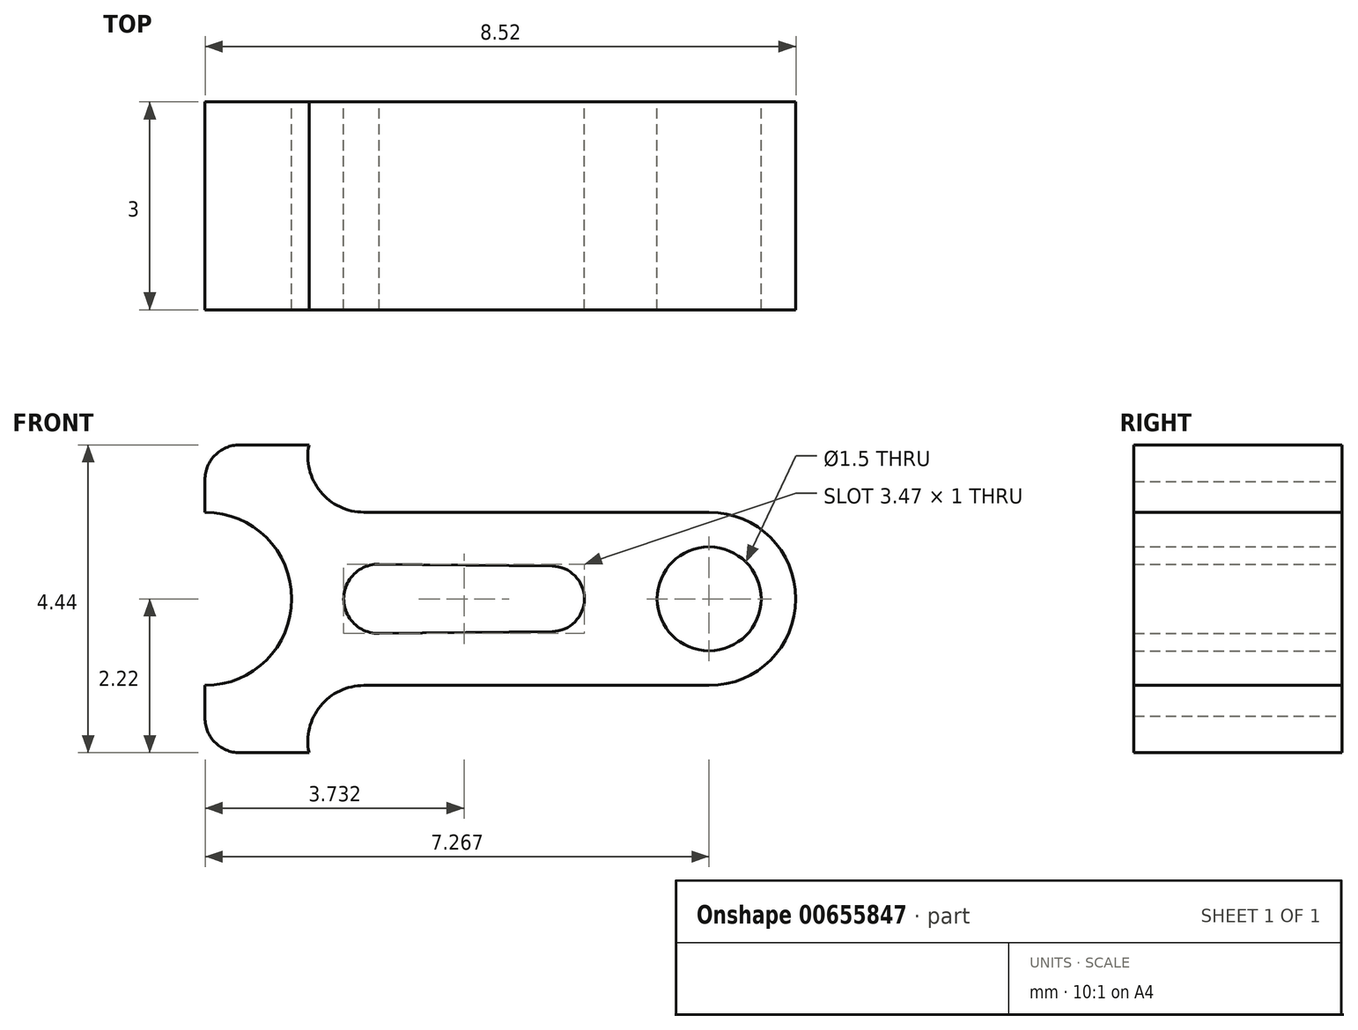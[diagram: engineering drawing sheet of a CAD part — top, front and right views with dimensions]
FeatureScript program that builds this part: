
annotation { "Feature Type Name" : "Feature", "Feature Type Description" : "" }
export const myFeature = defineFeature(function(context is Context, id is Id, definition is map)
    precondition{}
    {
        {
            var Q0;
            Q0=qCreatedBy(makeId("Front.planeOp"),FACE);
            var sketch = newSketch(context, id + "F0", { "sketchPlane" : qUnion([Q0])});
            skArc(sketch, "E0", {"start": v(-1.68, 0.5) * mm, "mid": v(-2.2, 0) * mm, "end": v(-1.68, -0.5) * mm});
            skArc(sketch, "E1", {"start": v(0.81, -0.47) * mm, "mid": v(1.28, 0) * mm, "end": v(0.81, 0.47) * mm});
            skLineSegment(sketch, "E2", {"start": v(-1.7, 0.5) * mm, "end": v(0.81, 0.47) * mm});
            skLineSegment(sketch, "E3", {"start": v(-1.7, -0.5) * mm, "end": v(0.81, -0.47) * mm});
            skCircle(sketch, "E4", {"center": v(3.08, 0) * mm, "radius": 0.75 * mm});
            skCircle(sketch, "E5", {"center": v(3.08, 0) * mm, "radius": 1.25 * mm});
            skArc(sketch, "E6", {"start": v(-4.2, -1.25) * mm, "mid": v(-2.94, 0) * mm, "end": v(-4.2, 1.25) * mm});
            skLineSegment(sketch, "E7", {"start": v(3.08, 1.25) * mm, "end": v(-1.9, 1.25) * mm});
            skLineSegment(sketch, "E8", {"start": v(-4.2, 1.25) * mm, "end": v(-4.2, 1.75) * mm});
            skArc(sketch, "E9", {"start": v(-3.7, 2.22) * mm, "mid": v(-4.06, 2.06) * mm, "end": v(-4.2, 1.7) * mm});
            skPoint(sketch, "E9.second.point", {"position": v(-3.2, 1.75) * mm});
            skPoint(sketch, "E9.third.point", {"position": v(-3.48, 2.17) * mm});
            skLineSegment(sketch, "E10", {"start": v(-3.7, 2.22) * mm, "end": v(-2.7, 2.22) * mm});
            skArc(sketch, "E11", {"start": v(-2.7, 2.22) * mm, "mid": v(-2.53, 1.55) * mm, "end": v(-1.9, 1.25) * mm});
            skPoint(sketch, "E11.second.point", {"position": v(-1.2, 1.66) * mm});
            skPoint(sketch, "E11.third.point", {"position": v(-2.68, 2.27) * mm});
            skLineSegment(sketch, "E12.MirrorCS", {"start": v(3.08, -1.25) * mm, "end": v(-1.9, -1.25) * mm});
            skArc(sketch, "E13.MirrorCS", {"start": v(-2.7, -2.22) * mm, "mid": v(-2.53, -1.55) * mm, "end": v(-1.9, -1.25) * mm});
            skLineSegment(sketch, "E14.MirrorCS", {"start": v(-3.7, -2.22) * mm, "end": v(-2.7, -2.22) * mm});
            skArc(sketch, "E15.MirrorCS", {"start": v(-3.7, -2.22) * mm, "mid": v(-4.06, -2.06) * mm, "end": v(-4.2, -1.7) * mm});
            skLineSegment(sketch, "E16.MirrorCS", {"start": v(-4.2, -1.25) * mm, "end": v(-4.2, -1.75) * mm});
            skSolve(sketch);
        }
        {
            var Q0;
            Q0 = qSketchRegion(id + "F0", true);
            extrude(context, id + "F1", {"entities" : qUnion([Q0]), "depth" : 3 * mm, "offsetDistance" : 25 * mm});
        }
    });
